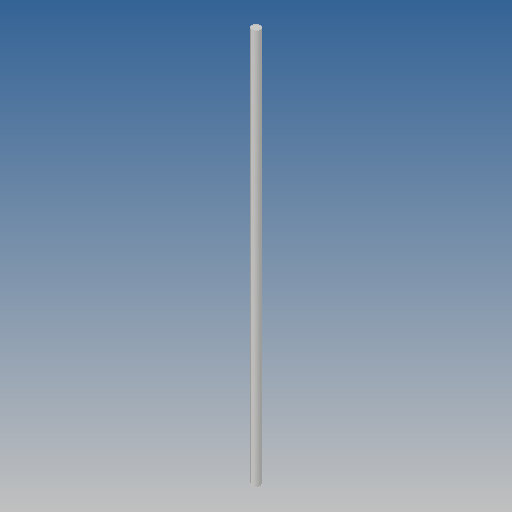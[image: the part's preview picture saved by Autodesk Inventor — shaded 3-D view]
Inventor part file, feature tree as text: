
AUTODESK INVENTOR PART (.ipt)
format: ipt  version: 2018 (Build 220112000, 112)  size: 75,264 bytes
history: native  units: mm
features: other x1, extrude x1, sketch x1
ambient origin geometry x8: Origin, YZ Plane, XZ Plane, XY Plane, X Axis, Y Axis, Z Axis, Center Point
bodies: Solid1 (feature_tree)
feature tree (3):
  other  "<userpath>\OneDrive\Objet3D\3DPrinter\Parameters.xlsx"
  extrude  "Extrusion1"  Depth=400.0mm
  sketch  "Sketch1"  dims[d0=8.0mm d1=400.0mm d2=0.0mm]
